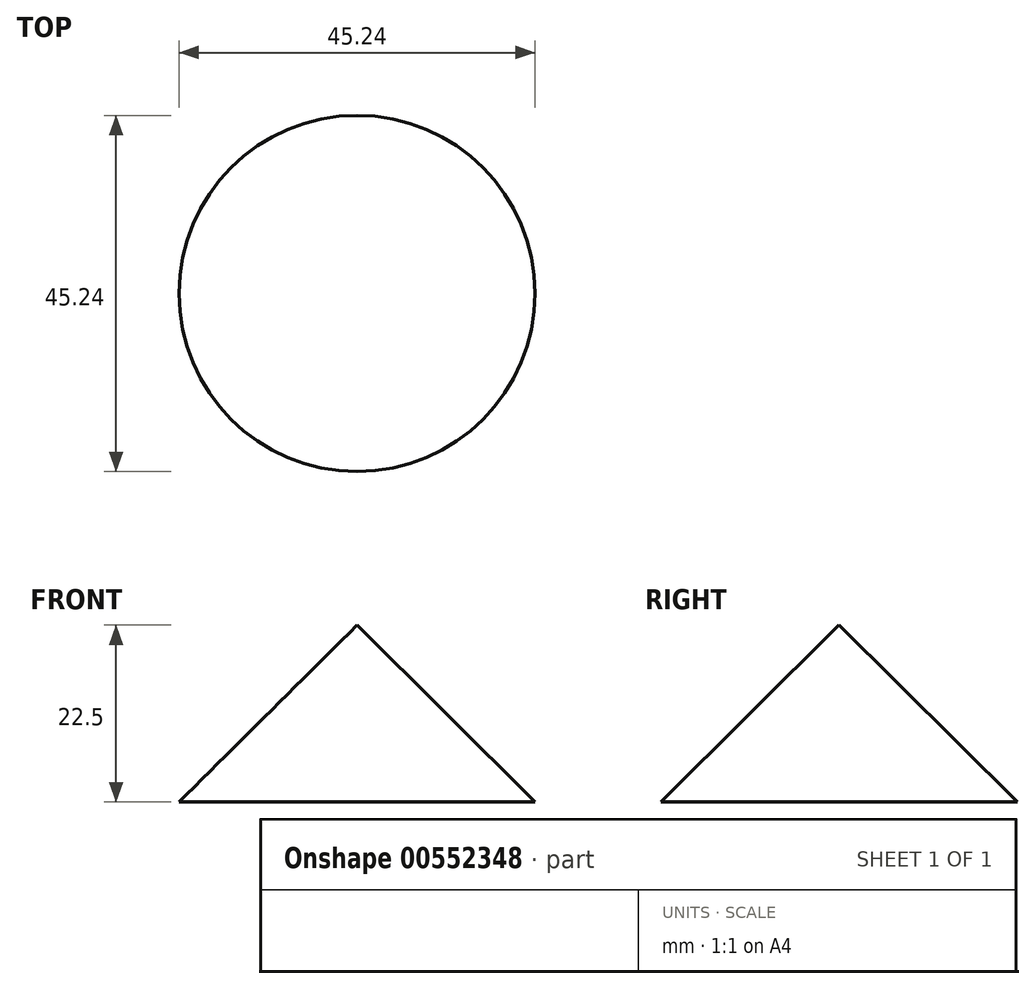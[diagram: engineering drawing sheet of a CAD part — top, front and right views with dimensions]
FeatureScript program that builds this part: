
annotation { "Feature Type Name" : "Feature", "Feature Type Description" : "" }
export const myFeature = defineFeature(function(context is Context, id is Id, definition is map)
    precondition{}
    {
        {
            var Q0;
            Q0=qCreatedBy(makeId("Front.planeOp"),FACE);
            var sketch = newSketch(context, id + "F0", { "sketchPlane" : qUnion([Q0])});
            skLineSegment(sketch, "E0", {"start": v(0, 0) * mm, "end": v(0, 55.95) * mm});
            skLineSegment(sketch, "E1", {"start": v(0, 55.95) * mm, "end": v(22.62, 33.45) * mm});
            skArc(sketch, "E2", {"start": v(0, 0) * mm, "mid": v(65.9, -20.2) * mm, "end": v(22.62, 33.45) * mm});
            skSolve(sketch);
        }
        {
            var Q0;
            Q0 = qSketchRegion(id + "F0", true);
            var Q1;
            Q1=sQuery(id+"F0.wireOp",EDGE,"E0");
            revolve(context, id + "F1", {"entities" : qUnion([Q0]), "axis" : qUnion([Q1]), "revolveType" : RevolveType.FULL});
        }
    });
